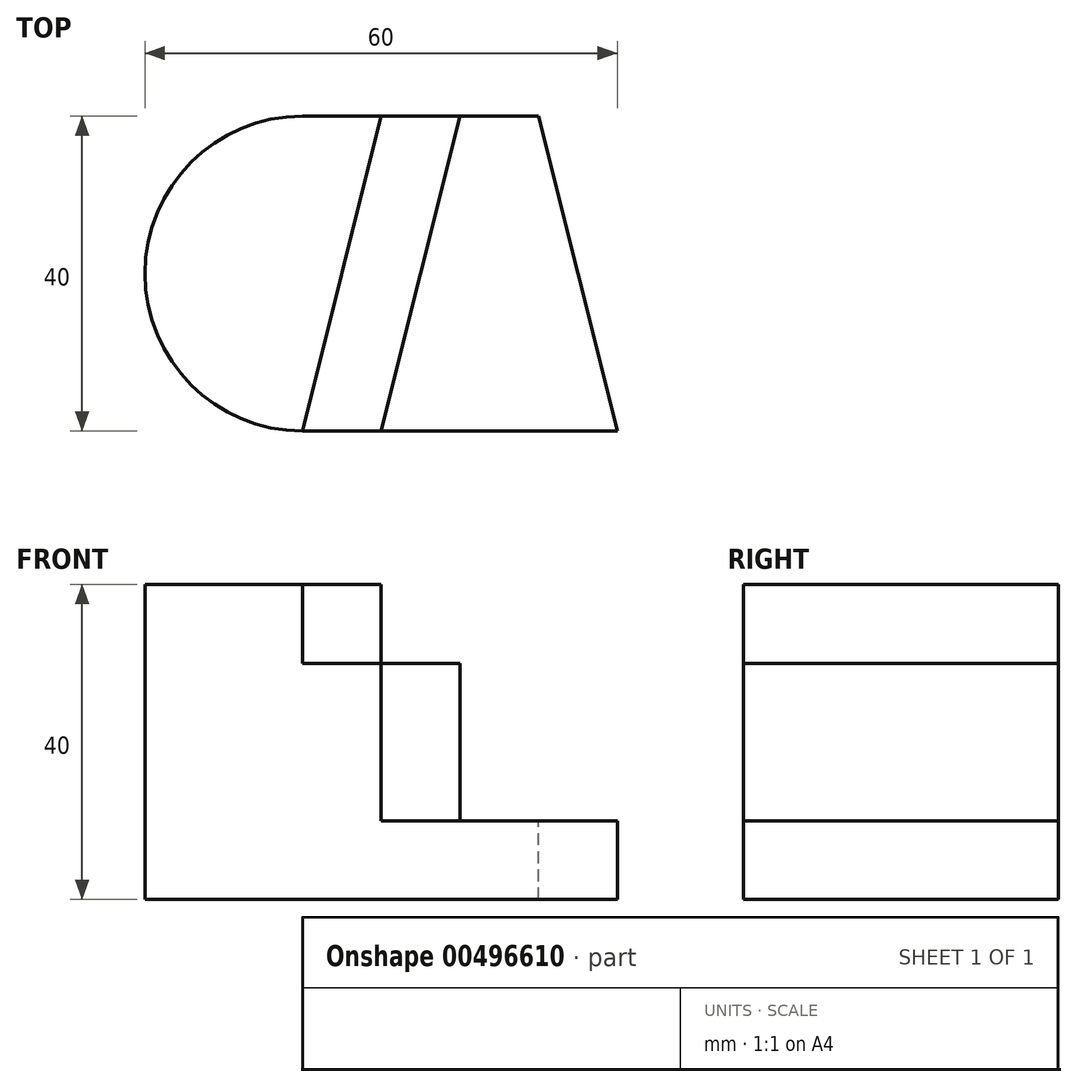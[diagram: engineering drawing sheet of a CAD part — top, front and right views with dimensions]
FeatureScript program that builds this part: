
annotation { "Feature Type Name" : "Feature", "Feature Type Description" : "" }
export const myFeature = defineFeature(function(context is Context, id is Id, definition is map)
    precondition{}
    {
        {
            var Q0;
            Q0=qCreatedBy(makeId("Top.planeOp"),FACE);
            var sketch = newSketch(context, id + "F0", { "sketchPlane" : qUnion([Q0])});
            skLineSegment(sketch, "E0", {"start": v(0, 0) * mm, "end": v(60, 0) * mm});
            skLineSegment(sketch, "E1", {"start": v(60, 0) * mm, "end": v(60, 40) * mm});
            skLineSegment(sketch, "E2", {"start": v(60, 40) * mm, "end": v(0, 40) * mm});
            skLineSegment(sketch, "E3", {"start": v(0, 40) * mm, "end": v(0, 0) * mm});
            skSolve(sketch);
        }
        {
            var Q0;
            Q0 = qSketchRegion(id + "F0", true);
            extrude(context, id + "F1", {"entities" : qUnion([Q0]), "depth" : 40 * mm});
        }
        {
            var Q0;
            Q0=makeQuery(id+"F1.opExtrude","SWEPT_EDGE",EDGE,{"disambiguationData":[OSD([sQuery(id+"F0.wireOp",EDGE,"E2"),sQuery(id+"F0.wireOp",EDGE,"E3")])]});
            var Q1;
            Q1=makeQuery(id+"F1.opExtrude","SWEPT_EDGE",EDGE,{"disambiguationData":[OSD([sQuery(id+"F0.wireOp",EDGE,"E0"),sQuery(id+"F0.wireOp",EDGE,"E3")])]});
            fillet(context, id + "F2", {"entities" : qUnion([Q0, Q1]), "radius" : 20 * mm, "tangentPropagation" : true, "allowEdgeOverflow" : false});
        }
        {
            var Q0;
            Q0=makeQuery(id+"F1.opExtrude","CAP_FACE",FACE,{"disambiguationData":[OSD([sQuery(id+"F0.wireOp",EDGE,"E0"),sQuery(id+"F0.wireOp",EDGE,"E1"),sQuery(id+"F0.wireOp",EDGE,"E2"),sQuery(id+"F0.wireOp",EDGE,"E3")])],"isStart":false});
            var sketch = newSketch(context, id + "F3", { "sketchPlane" : qUnion([Q0])});
            skLineSegment(sketch, "E4", {"start": v(60, 40) * mm, "end": v(50, 40) * mm});
            skLineSegment(sketch, "E5", {"start": v(50, 40) * mm, "end": v(60, 0) * mm});
            skLineSegment(sketch, "E6", {"start": v(60, 0) * mm, "end": v(60, 40) * mm});
            skSolve(sketch);
        }
        {
            var Q0;
            Q0=makeQuery(id+"F3.imprint","IMPRINT",FACE,{"disambiguationData":[TD([[makeQuery(id+"F3.imprint","IMPRINT",EDGE,{"derivedFrom":sQuery(id+"F3.wireOp",EDGE,"E4")}),1.0]])]});
            extrude(context, id + "F4", {"entities" : qUnion([Q0]), "operationType" : NewBodyOperationType.REMOVE, "oppositeDirection" : true, "depth" : 40 * mm});
        }
        {
            var Q0;
            Q0=makeQuery(id+"F1.opExtrude","CAP_FACE",FACE,{"disambiguationData":[OSD([sQuery(id+"F0.wireOp",EDGE,"E0"),sQuery(id+"F0.wireOp",EDGE,"E1"),sQuery(id+"F0.wireOp",EDGE,"E2"),sQuery(id+"F0.wireOp",EDGE,"E3")])],"isStart":false});
            var sketch = newSketch(context, id + "F5", { "sketchPlane" : qUnion([Q0])});
            skLineSegment(sketch, "E7", {"start": v(50, 40) * mm, "end": v(40, 40) * mm});
            skLineSegment(sketch, "E8", {"start": v(60, 0) * mm, "end": v(30, 0) * mm});
            skLineSegment(sketch, "E9", {"start": v(30, 0) * mm, "end": v(40, 40) * mm});
            skSolve(sketch);
        }
        {
            var Q0;
            Q0=makeQuery(id+"F5.imprint","IMPRINT",FACE,{"disambiguationData":[TD([[makeQuery(id+"F5.imprint","IMPRINT",EDGE,{"derivedFrom":sQuery(id+"F5.wireOp",EDGE,"E7")}),1.0]])]});
            extrude(context, id + "F6", {"entities" : qUnion([Q0]), "operationType" : NewBodyOperationType.REMOVE, "oppositeDirection" : true, "depth" : 30 * mm});
        }
        {
            var Q0;
            Q0=makeQuery(id+"F1.opExtrude","CAP_FACE",FACE,{"disambiguationData":[OSD([sQuery(id+"F0.wireOp",EDGE,"E0"),sQuery(id+"F0.wireOp",EDGE,"E1"),sQuery(id+"F0.wireOp",EDGE,"E2"),sQuery(id+"F0.wireOp",EDGE,"E3")])],"isStart":false});
            var sketch = newSketch(context, id + "F7", { "sketchPlane" : qUnion([Q0])});
            skLineSegment(sketch, "E10", {"start": v(40, 40) * mm, "end": v(30, 40) * mm});
            skLineSegment(sketch, "E11", {"start": v(30, 0) * mm, "end": v(20, 0) * mm});
            skLineSegment(sketch, "E12", {"start": v(20, 0) * mm, "end": v(30, 40) * mm});
            skLineSegment(sketch, "E13", {"start": v(40, 40) * mm, "end": v(30, 0) * mm});
            skSolve(sketch);
        }
        {
            var Q0;
            Q0 = qSketchRegion(id + "F7", true);
            extrude(context, id + "F8", {"entities" : qUnion([Q0]), "operationType" : NewBodyOperationType.REMOVE, "oppositeDirection" : true, "depth" : 10 * mm});
        }
    });
